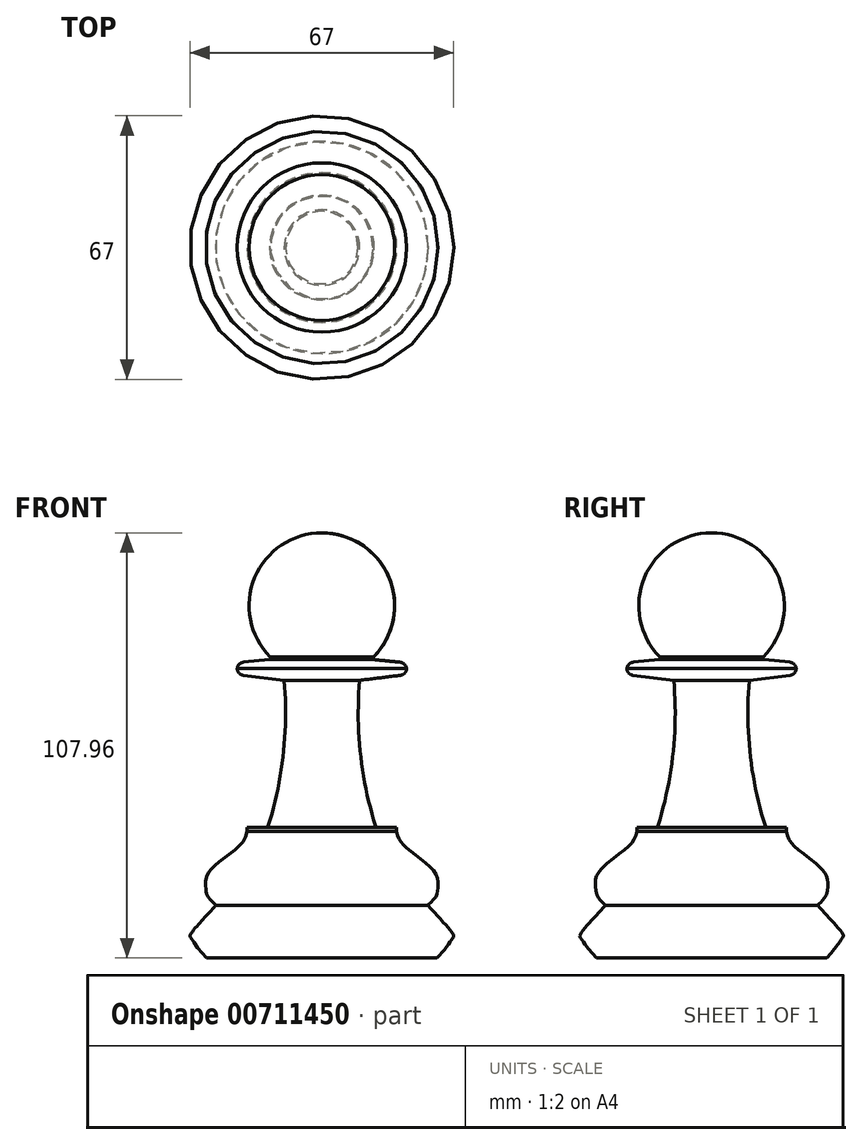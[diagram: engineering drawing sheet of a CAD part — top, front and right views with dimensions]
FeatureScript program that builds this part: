
annotation { "Feature Type Name" : "Feature", "Feature Type Description" : "" }
export const myFeature = defineFeature(function(context is Context, id is Id, definition is map)
    precondition{}
    {
        {
            var Q0;
            Q0=qCreatedBy(makeId("Front.planeOp"),FACE);
            var sketch = newSketch(context, id + "F0", { "sketchPlane" : qUnion([Q0])});
            skLineSegment(sketch, "E0", {"start": v(0, 70.83) * mm, "end": v(0, -73.84) * mm, "construction": true});
            skArc(sketch, "E1", {"start": v(13.16, -13) * mm, "mid": v(17.07, 7.13) * mm, "end": v(0, 18.5) * mm});
            skPoint(sketch, "E2", {"position": v(0, -14) * mm});
            skLineSegment(sketch, "E3", {"start": v(9.6, -18.96) * mm, "end": v(19.94, -17.68) * mm});
            skLineSegment(sketch, "E4", {"start": v(13.29, -13.72) * mm, "end": v(19.9, -14.35) * mm});
            skPoint(sketch, "E5.visualSharp", {"position": v(21.3, -14.49) * mm});
            skArc(sketch, "E5.filletArc", {"start": v(21.52, -15.99) * mm, "mid": v(21, -14.88) * mm, "end": v(19.9, -14.35) * mm});
            skPoint(sketch, "E6.visualSharp", {"position": v(21.3, -17.5) * mm});
            skArc(sketch, "E6.filletArc", {"start": v(19.94, -17.68) * mm, "mid": v(21.03, -17.12) * mm, "end": v(21.52, -15.99) * mm});
            skPoint(sketch, "E7.orphan", {"position": v(21.3, -14) * mm});
            skArc(sketch, "E8", {"start": v(13.16, -13) * mm, "mid": v(13.06, -13.39) * mm, "end": v(13.29, -13.72) * mm});
            skPoint(sketch, "E9.orphan", {"position": v(21.3, -18) * mm});
            skArc(sketch, "E10", {"start": v(9.6, -18.96) * mm, "mid": v(9.8, -37.66) * mm, "end": v(13.64, -55.96) * mm});
            skLineSegment(sketch, "E11", {"start": v(-79.05, -57.3) * mm, "end": v(19, -57.3) * mm});
            skLineSegment(sketch, "E12", {"start": v(14.12, -56.3) * mm, "end": v(19.18, -56.3) * mm});
            skLineSegment(sketch, "E13", {"start": v(19, -55.85) * mm, "end": v(19, -57.3) * mm});
            skPoint(sketch, "E14.visualSharp", {"position": v(13.75, -56.3) * mm});
            skArc(sketch, "E14.filletArc", {"start": v(13.64, -55.96) * mm, "mid": v(13.82, -56.21) * mm, "end": v(14.12, -56.3) * mm});
            skArc(sketch, "E15", {"start": v(19, -55.85) * mm, "mid": v(17.8, -55.38) * mm, "end": v(16.92, -56.3) * mm});
            skLineSegment(sketch, "E16", {"start": v(-90, -89.46) * mm, "end": v(29.3, -89.46) * mm});
            skFitSpline(sketch, "E17", {"points": [v(19, -57.3) * mm, v(21.21, -61.27) * mm, v(28.81, -67.9) * mm, v(29.5, -71.65) * mm, v(28.7, -74.29) * mm, v(26.96, -76.18) * mm], "startDerivative": vector(5.85, -27.07) * mm, "endDerivative": vector(2.95, -0.8) * mm});
            skLineSegment(sketch, "E18", {"start": v(27.5, -63.43) * mm, "end": v(27.5, -92.85) * mm, "construction": true});
            skFitSpline(sketch, "E19", {"points": [v(26.96, -76.18) * mm, v(33.1, -83.07) * mm, v(33.5, -83.9) * mm, v(33.15, -84.58) * mm, v(29.3, -89.46) * mm], "startDerivative": vector(18.65, -20.18) * mm, "endDerivative": vector(-14.85, -14.43) * mm});
            skLineSegment(sketch, "E20", {"start": v(0, 18.5) * mm, "end": v(0, -89.46) * mm});
            skLineSegment(sketch, "E21", {"start": v(0, -89.46) * mm, "end": v(29.3, -89.46) * mm});
            skSolve(sketch);
        }
        {
            var Q0;
            {var subQ4=sQuery(id+"F0.wireOp",EDGE,"E17");Q0=makeQuery(id+"F0.imprint","IMPRINT",FACE,{"disambiguationData":[TD([[makeQuery(id+"F0.imprint","IMPRINT",EDGE,{"derivedFrom":subQ4}),-1.0]])]});}
            var Q1;
            {var subQ5=sQuery(id+"F0.wireOp",EDGE,"E1");Q1=makeQuery(id+"F0.imprint","IMPRINT",FACE,{"disambiguationData":[TD([[makeQuery(id+"F0.imprint","IMPRINT",EDGE,{"derivedFrom":subQ5}),1.0]])]});}
            var Q2;
            Q2=sQuery(id+"F0.wireOp",EDGE,"E0");
            revolve(context, id + "F1", {"surfaceOperationType" : NewSurfaceOperationType.NEW, "entities" : qUnion([Q0, Q1]), "axis" : qUnion([Q2]), "revolveType" : RevolveType.FULL});
        }
    });
